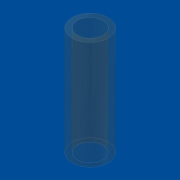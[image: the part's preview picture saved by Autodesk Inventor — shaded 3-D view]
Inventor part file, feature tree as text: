
AUTODESK INVENTOR PART (.ipt)
format: ipt  version: unknown  size: 155,136 bytes
history: native  units: mm
features: extrude x1, sketch x1
ambient origin geometry x8: Origin, YZ Plane, XZ Plane, XY Plane, X Axis, Y Axis, Z Axis, Center Point
feature tree (2):
  extrude  "Extrusion1"  Depth=7.1mm
  sketch  "Sketch1"  dims[d0=10.0mm d1=7.1mm d2=30.0mm d3=0.0mm]
